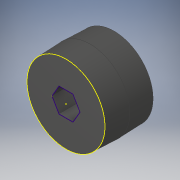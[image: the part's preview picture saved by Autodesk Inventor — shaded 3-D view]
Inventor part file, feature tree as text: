
AUTODESK INVENTOR PART (.ipt)
format: ipt  version: 2017 (Build 210142000, 142)  size: 691,200 bytes
history: native  units: in
note: dims shown in document units (in); Inventor stores cm internally (conversion verified against a paired STEP export)
features: sketch x1, projected_geometry x1, other x1
ambient origin geometry x8: Origin, YZ Plane, XZ Plane, XY Plane, X Axis, Y Axis, Z Axis, Center Point
bodies: Solid1 (feature_tree)
feature tree (3):
  sketch  "Sketch1"
  projected_geometry  "Projected Loop1"
  other  "_2in Wheel Intergrated Hub Design_-_CirPattern1_"
